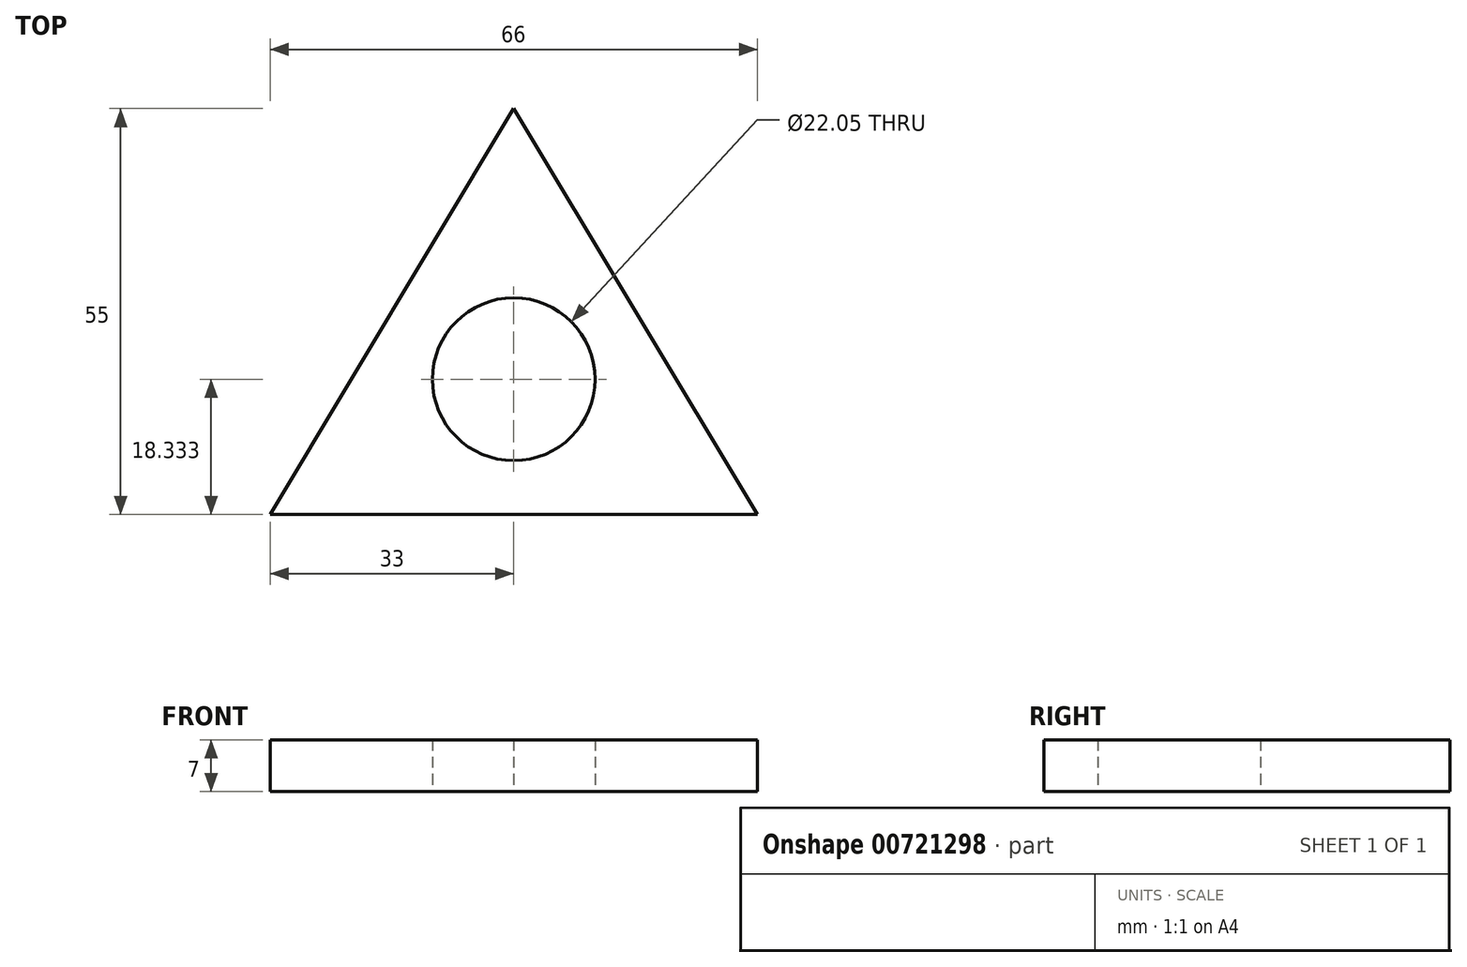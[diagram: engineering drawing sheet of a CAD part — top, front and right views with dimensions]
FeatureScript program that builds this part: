
annotation { "Feature Type Name" : "Feature", "Feature Type Description" : "" }
export const myFeature = defineFeature(function(context is Context, id is Id, definition is map)
    precondition{}
    {
        {
            var Q0;
            Q0=qCreatedBy(makeId("Top.planeOp"),FACE);
            var sketch = newSketch(context, id + "F0", { "sketchPlane" : qUnion([Q0])});
            skLineSegment(sketch, "E0", {"start": v(0, -22) * mm, "end": v(33, -22) * mm});
            skLineSegment(sketch, "E1", {"start": v(0, -22) * mm, "end": v(-33, -22) * mm});
            skLineSegment(sketch, "E2", {"start": v(0, 33) * mm, "end": v(-33, -22) * mm});
            skLineSegment(sketch, "E3", {"start": v(0, 33) * mm, "end": v(33, -22) * mm});
            skCircle(sketch, "E4", {"center": v(0, -3.67) * mm, "radius": 11.03 * mm});
            skSolve(sketch);
        }
        {
            var Q0;
            Q0=makeQuery(id+"F0.imprint","IMPRINT",FACE,{"disambiguationData":[TD([[makeQuery(id+"F0.imprint","IMPRINT",EDGE,{"derivedFrom":sQuery(id+"F0.wireOp",EDGE,"E0")}),1.0]])]});
            extrude(context, id + "F1", {"entities" : qUnion([Q0]), "depth" : 7 * mm, "offsetDistance" : 25 * mm});
        }
    });
